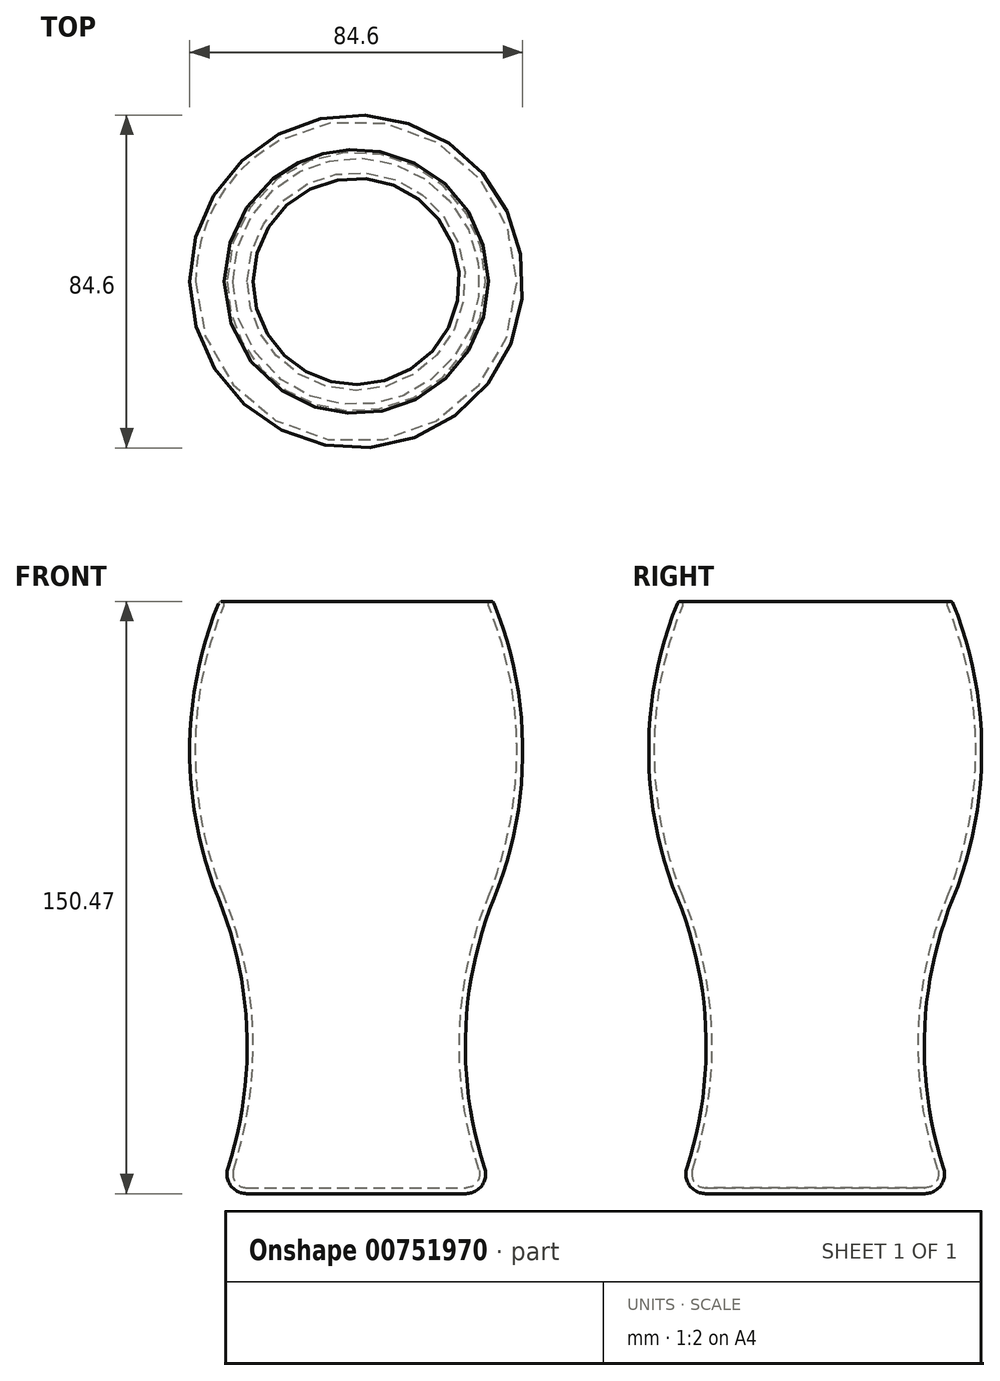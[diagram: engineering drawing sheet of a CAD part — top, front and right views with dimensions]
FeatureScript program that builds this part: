
annotation { "Feature Type Name" : "Feature", "Feature Type Description" : "" }
export const myFeature = defineFeature(function(context is Context, id is Id, definition is map)
    precondition{}
    {
        {
            var Q0;
            Q0=qCreatedBy(makeId("Right.planeOp"),FACE);
            var sketch = newSketch(context, id + "F0", { "sketchPlane" : qUnion([Q0])});
            skLineSegment(sketch, "E0", {"start": v(0, 0) * mm, "end": v(-27.86, 0) * mm});
            skPoint(sketch, "E1", {"position": v(-35, 75) * mm});
            skArc(sketch, "E2", {"start": v(-35, 150) * mm, "mid": v(-42.3, 112.5) * mm, "end": v(-35, 75) * mm});
            skArc(sketch, "E3", {"start": v(-32.61, 6.55) * mm, "mid": v(-27.76, 40.98) * mm, "end": v(-35, 75) * mm});
            skPoint(sketch, "E4.visualSharp", {"position": v(-35, 0) * mm});
            skArc(sketch, "E4.filletArc", {"start": v(-32.61, 6.55) * mm, "mid": v(-31.9, 2.06) * mm, "end": v(-27.86, 0) * mm});
            skArc(sketch, "E5.0", {"start": v(-33.6, 149.44) * mm, "mid": v(-40.8, 112.5) * mm, "end": v(-33.6, 75.56) * mm});
            skArc(sketch, "E5.1", {"start": v(-31.19, 6.08) * mm, "mid": v(-26.26, 41.04) * mm, "end": v(-33.6, 75.56) * mm});
            skArc(sketch, "E5.2", {"start": v(-31.19, 6.08) * mm, "mid": v(-30.7, 2.94) * mm, "end": v(-27.86, 1.5) * mm});
            skLineSegment(sketch, "E5.3", {"start": v(0, 1.5) * mm, "end": v(-27.86, 1.5) * mm});
            skArc(sketch, "E6", {"start": v(-35, 150) * mm, "mid": v(-34.02, 150.41) * mm, "end": v(-33.6, 149.44) * mm});
            skSolve(sketch);
        }
        {
            var Q0;
            Q0=qCreatedBy(makeId("Right.planeOp"),FACE);
            var sketch = newSketch(context, id + "F1", { "sketchPlane" : qUnion([Q0])});
            skLineSegment(sketch, "E7", {"start": v(0, 1.5) * mm, "end": v(0, 0) * mm});
            skSolve(sketch);
        }
        {
            var Q0;
            Q0=sQuery(id+"F0.wireOp",EDGE,"E3");
            var Q1;
            Q1=sQuery(id+"F0.wireOp",EDGE,"E2");
            var Q2;
            Q2=sQuery(id+"F0.wireOp",EDGE,"E5.0");
            var Q3;
            Q3=sQuery(id+"F0.wireOp",EDGE,"E5.1");
            var Q4;
            Q4=sQuery(id+"F0.wireOp",EDGE,"E6");
            var Q5;
            Q5=sQuery(id+"F0.wireOp",EDGE,"E4.filletArc");
            var Q6;
            Q6=sQuery(id+"F0.wireOp",EDGE,"E5.2");
            var Q7;
            Q7=sQuery(id+"F0.wireOp",EDGE,"E0");
            var Q8;
            Q8=sQuery(id+"F0.wireOp",EDGE,"E5.3");
            var Q9;
            Q9=sQuery(id+"F1.wireOp",EDGE,"E7");
            revolve(context, id + "F2", {"bodyType" : ToolBodyType.SURFACE, "surfaceOperationType" : NewSurfaceOperationType.NEW, "surfaceEntities" : qUnion([Q0, Q1, Q2, Q3, Q4, Q5, Q6, Q7, Q8]), "axis" : qUnion([Q9]), "revolveType" : RevolveType.FULL});
        }
    });
